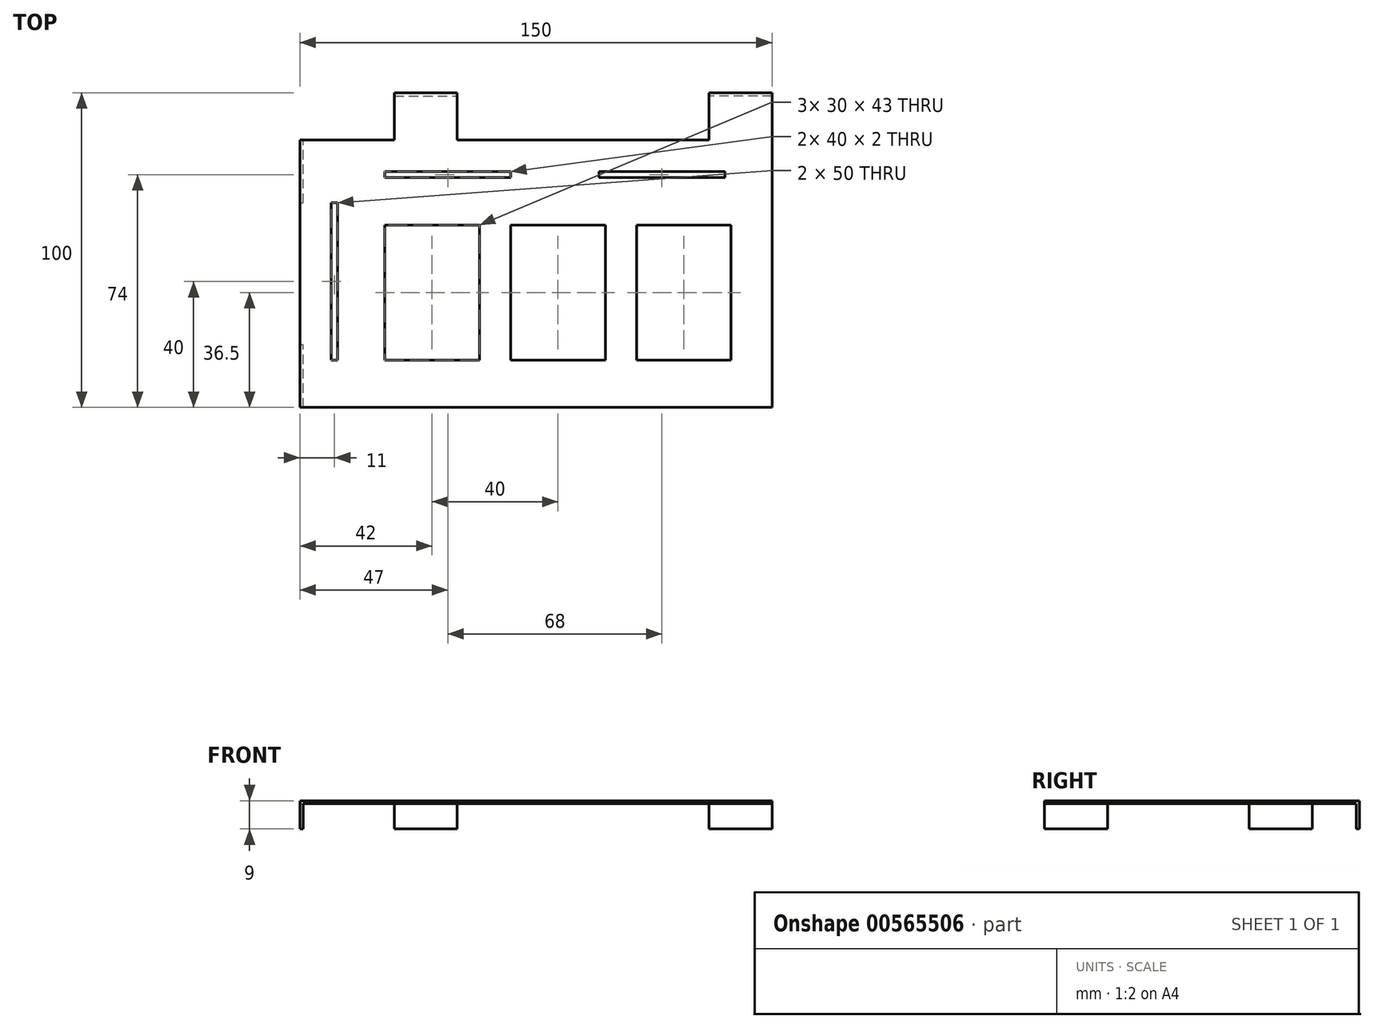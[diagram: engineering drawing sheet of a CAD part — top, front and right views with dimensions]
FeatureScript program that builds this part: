
annotation { "Feature Type Name" : "Feature", "Feature Type Description" : "" }
export const myFeature = defineFeature(function(context is Context, id is Id, definition is map)
    precondition{}
    {
        {
            var Q0;
            Q0=qCreatedBy(makeId("Top.planeOp"),FACE);
            var sketch = newSketch(context, id + "F0", { "sketchPlane" : qUnion([Q0])});
            skLineSegment(sketch, "E0.bottom", {"start": v(75, 50) * mm, "end": v(-75, 50) * mm});
            skLineSegment(sketch, "E0.top", {"start": v(75, -50) * mm, "end": v(-75, -50) * mm});
            skLineSegment(sketch, "E0.left", {"start": v(75, 50) * mm, "end": v(75, -50) * mm});
            skLineSegment(sketch, "E0.right", {"start": v(-75, 50) * mm, "end": v(-75, -50) * mm});
            skPoint(sketch, "E0.middle", {"position": v(0, 0) * mm});
            skSolve(sketch);
        }
        {
            var Q0;
            Q0 = qSketchRegion(id + "F0", true);
            extrude(context, id + "F1", {"entities" : qUnion([Q0]), "depth" : 1 * mm, "offsetDistance" : 25 * mm});
        }
        {
            var Q0;
            Q0=makeQuery(id+"F1.opExtrude","CAP_FACE",FACE,{"disambiguationData":[OSD([sQuery(id+"F0.wireOp",EDGE,"E0.bottom"),sQuery(id+"F0.wireOp",EDGE,"E0.top"),sQuery(id+"F0.wireOp",EDGE,"E0.left"),sQuery(id+"F0.wireOp",EDGE,"E0.right")])],"isStart":false});
            var sketch = newSketch(context, id + "F2", { "sketchPlane" : qUnion([Q0])});
            skLineSegment(sketch, "E1.bottom", {"start": v(-45, 50) * mm, "end": v(-75, 50) * mm});
            skLineSegment(sketch, "E1.top", {"start": v(-45, 35) * mm, "end": v(-75, 35) * mm});
            skLineSegment(sketch, "E1.left", {"start": v(-45, 50) * mm, "end": v(-45, 35) * mm});
            skLineSegment(sketch, "E1.right", {"start": v(-75, 50) * mm, "end": v(-75, 35) * mm});
            skLineSegment(sketch, "E2.bottom", {"start": v(-25, 35) * mm, "end": v(55, 35) * mm});
            skLineSegment(sketch, "E2.top", {"start": v(-25, 50) * mm, "end": v(55, 50) * mm});
            skLineSegment(sketch, "E2.left", {"start": v(-25, 35) * mm, "end": v(-25, 50) * mm});
            skLineSegment(sketch, "E2.right", {"start": v(55, 35) * mm, "end": v(55, 50) * mm});
            skSolve(sketch);
        }
        {
            var Q0;
            Q0 = qSketchRegion(id + "F2", true);
            extrude(context, id + "F3", {"entities" : qUnion([Q0]), "operationType" : NewBodyOperationType.REMOVE, "endBound" : BoundingType.THROUGH_ALL, "oppositeDirection" : true, "depth" : 25 * mm, "offsetDistance" : 25 * mm});
        }
        {
            var Q0;
            Q0=makeQuery(id+"F1.opExtrude","CAP_FACE",FACE,{"disambiguationData":[OSD([sQuery(id+"F0.wireOp",EDGE,"E0.bottom"),sQuery(id+"F0.wireOp",EDGE,"E0.top"),sQuery(id+"F0.wireOp",EDGE,"E0.left"),sQuery(id+"F0.wireOp",EDGE,"E0.right")])],"isStart":true});
            var sketch = newSketch(context, id + "F4", { "sketchPlane" : qUnion([Q0])});
            skLineSegment(sketch, "E3.bottom", {"start": v(-75, -15) * mm, "end": v(-74, -15) * mm});
            skLineSegment(sketch, "E3.top", {"start": v(-75, -35) * mm, "end": v(-74, -35) * mm});
            skLineSegment(sketch, "E3.left", {"start": v(-75, -15) * mm, "end": v(-75, -35) * mm});
            skLineSegment(sketch, "E3.right", {"start": v(-74, -15) * mm, "end": v(-74, -35) * mm});
            skLineSegment(sketch, "E4.bottom", {"start": v(-45, -50) * mm, "end": v(-25, -50) * mm});
            skLineSegment(sketch, "E4.top", {"start": v(-45, -49) * mm, "end": v(-25, -49) * mm});
            skLineSegment(sketch, "E4.left", {"start": v(-45, -50) * mm, "end": v(-45, -49) * mm});
            skLineSegment(sketch, "E4.right", {"start": v(-25, -50) * mm, "end": v(-25, -49) * mm});
            skLineSegment(sketch, "E5.bottom", {"start": v(75, -50) * mm, "end": v(55, -50) * mm});
            skLineSegment(sketch, "E5.top", {"start": v(75, -49) * mm, "end": v(55, -49) * mm});
            skLineSegment(sketch, "E5.left", {"start": v(75, -50) * mm, "end": v(75, -49) * mm});
            skLineSegment(sketch, "E5.right", {"start": v(55, -50) * mm, "end": v(55, -49) * mm});
            skLineSegment(sketch, "E6.bottom", {"start": v(-75, 50) * mm, "end": v(-74, 50) * mm});
            skLineSegment(sketch, "E6.top", {"start": v(-75, 30) * mm, "end": v(-74, 30) * mm});
            skLineSegment(sketch, "E6.left", {"start": v(-75, 50) * mm, "end": v(-75, 30) * mm});
            skLineSegment(sketch, "E6.right", {"start": v(-74, 50) * mm, "end": v(-74, 30) * mm});
            skSolve(sketch);
        }
        {
            var Q0;
            Q0 = qSketchRegion(id + "F4", true);
            extrude(context, id + "F5", {"entities" : qUnion([Q0]), "operationType" : NewBodyOperationType.ADD, "depth" : 8 * mm, "offsetDistance" : 25 * mm});
        }
        {
            var Q0;
            Q0=makeQuery(id+"F1.opExtrude","CAP_FACE",FACE,{"disambiguationData":[OSD([sQuery(id+"F0.wireOp",EDGE,"E0.bottom"),sQuery(id+"F0.wireOp",EDGE,"E0.top"),sQuery(id+"F0.wireOp",EDGE,"E0.left"),sQuery(id+"F0.wireOp",EDGE,"E0.right")])],"isStart":false});
            var sketch = newSketch(context, id + "F6", { "sketchPlane" : qUnion([Q0])});
            skLineSegment(sketch, "E7.bottom", {"start": v(-65, 15) * mm, "end": v(-63, 15) * mm});
            skLineSegment(sketch, "E7.top", {"start": v(-65, -35) * mm, "end": v(-63, -35) * mm});
            skLineSegment(sketch, "E7.left", {"start": v(-65, 15) * mm, "end": v(-65, -35) * mm});
            skLineSegment(sketch, "E7.right", {"start": v(-63, 15) * mm, "end": v(-63, -35) * mm});
            skLineSegment(sketch, "E8.bottom", {"start": v(-48, 25) * mm, "end": v(-8, 25) * mm});
            skLineSegment(sketch, "E8.top", {"start": v(-48, 23) * mm, "end": v(-8, 23) * mm});
            skLineSegment(sketch, "E8.left", {"start": v(-48, 25) * mm, "end": v(-48, 23) * mm});
            skLineSegment(sketch, "E8.right", {"start": v(-8, 25) * mm, "end": v(-8, 23) * mm});
            skLineSegment(sketch, "E9.bottom", {"start": v(20, 25) * mm, "end": v(60, 25) * mm});
            skLineSegment(sketch, "E9.top", {"start": v(20, 23) * mm, "end": v(60, 23) * mm});
            skLineSegment(sketch, "E9.left", {"start": v(20, 25) * mm, "end": v(20, 23) * mm});
            skLineSegment(sketch, "E9.right", {"start": v(60, 25) * mm, "end": v(60, 23) * mm});
            skLineSegment(sketch, "E10.bottom", {"start": v(-48, 8) * mm, "end": v(-18, 8) * mm});
            skLineSegment(sketch, "E10.top", {"start": v(-48, -35) * mm, "end": v(-18, -35) * mm});
            skLineSegment(sketch, "E10.left", {"start": v(-48, 8) * mm, "end": v(-48, -35) * mm});
            skLineSegment(sketch, "E10.right", {"start": v(-18, 8) * mm, "end": v(-18, -35) * mm});
            skLineSegment(sketch, "E11.1.0.0", {"start": v(-8, -35) * mm, "end": v(22, -35) * mm});
            skLineSegment(sketch, "E11.1.0.1", {"start": v(-8, 8) * mm, "end": v(-8, -35) * mm});
            skLineSegment(sketch, "E11.1.0.2", {"start": v(-8, 8) * mm, "end": v(22, 8) * mm});
            skLineSegment(sketch, "E11.1.0.3", {"start": v(22, 8) * mm, "end": v(22, -35) * mm});
            skLineSegment(sketch, "E11.2.0.0", {"start": v(32, -35) * mm, "end": v(62, -35) * mm});
            skLineSegment(sketch, "E11.2.0.1", {"start": v(32, 8) * mm, "end": v(32, -35) * mm});
            skLineSegment(sketch, "E11.2.0.2", {"start": v(32, 8) * mm, "end": v(62, 8) * mm});
            skLineSegment(sketch, "E11.2.0.3", {"start": v(62, 8) * mm, "end": v(62, -35) * mm});
            skLineSegment(sketch, "E11.direction1", {"start": v(-48, -35) * mm, "end": v(-8, -35) * mm, "construction": true});
            skSolve(sketch);
        }
        {
            var Q0;
            Q0 = qSketchRegion(id + "F6", true);
            extrude(context, id + "F7", {"entities" : qUnion([Q0]), "operationType" : NewBodyOperationType.REMOVE, "endBound" : BoundingType.THROUGH_ALL, "oppositeDirection" : true, "depth" : 25 * mm, "offsetDistance" : 25 * mm});
        }
    });
